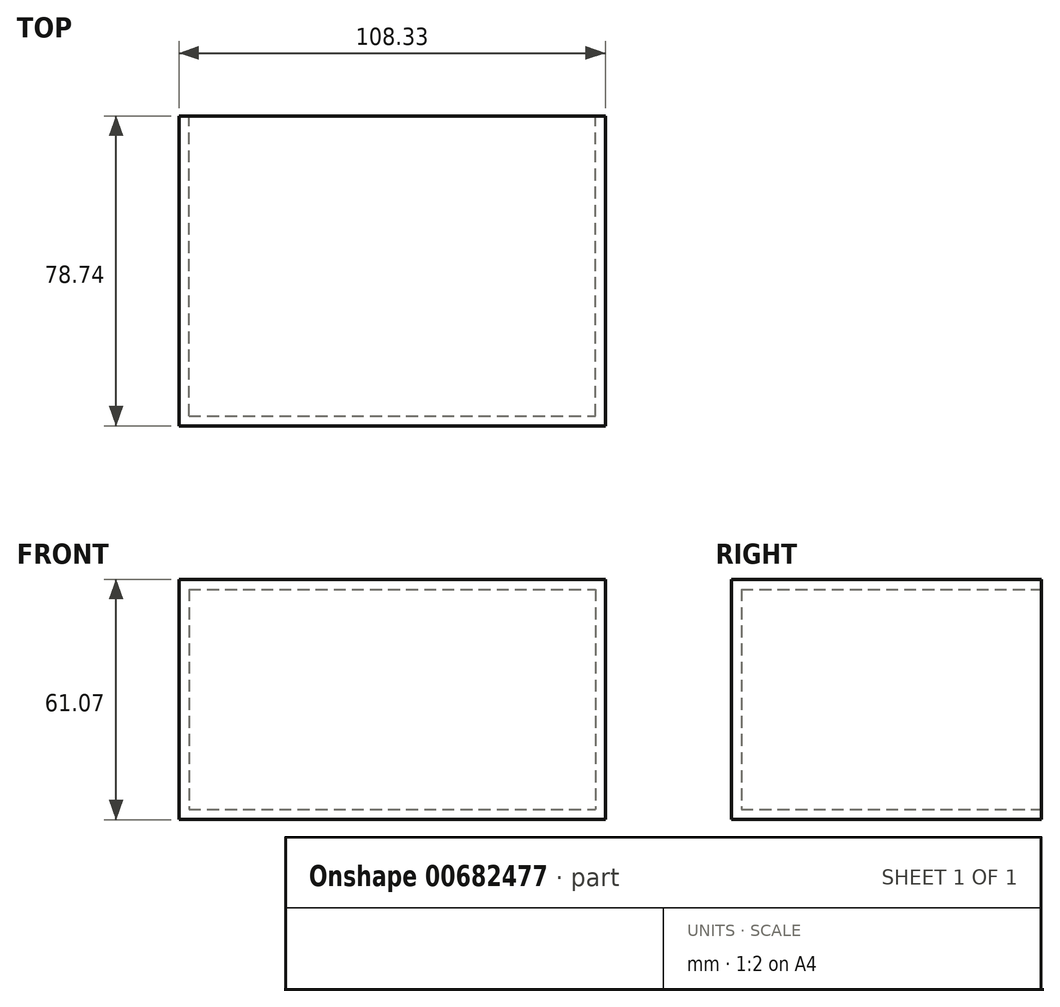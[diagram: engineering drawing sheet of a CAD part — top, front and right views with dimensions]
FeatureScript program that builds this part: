
annotation { "Feature Type Name" : "Feature", "Feature Type Description" : "" }
export const myFeature = defineFeature(function(context is Context, id is Id, definition is map)
    precondition{}
    {
        {
            var Q0;
            Q0=qCreatedBy(makeId("Front.planeOp"),FACE);
            var sketch = newSketch(context, id + "F0", { "sketchPlane" : qUnion([Q0])});
            skLineSegment(sketch, "E0.bottom", {"start": v(-61.13, 40) * mm, "end": v(42.12, 40) * mm});
            skLineSegment(sketch, "E0.top", {"start": v(-61.13, -15.98) * mm, "end": v(42.12, -15.98) * mm});
            skLineSegment(sketch, "E0.left", {"start": v(-61.13, 40) * mm, "end": v(-61.13, -15.98) * mm});
            skLineSegment(sketch, "E0.right", {"start": v(42.12, 40) * mm, "end": v(42.12, -15.98) * mm});
            skSolve(sketch);
        }
        {
            var Q0;
            Q0=makeQuery(id+"F0.imprint","IMPRINT",FACE,{"disambiguationData":[TD([[makeQuery(id+"F0.imprint","IMPRINT",EDGE,{"derivedFrom":sQuery(id+"F0.wireOp",EDGE,"E0.bottom")}),-1.0]])]});
            extrude(context, id + "F1", {"entities" : qUnion([Q0]), "depth" : 76.2 * mm, "offsetDistance" : 25.4 * mm});
        }
        {
            var Q0;
            Q0=makeQuery(id+"F1.opExtrude","CAP_FACE",FACE,{"disambiguationData":[OSD([sQuery(id+"F0.wireOp",EDGE,"E0.bottom"),sQuery(id+"F0.wireOp",EDGE,"E0.top"),sQuery(id+"F0.wireOp",EDGE,"E0.left"),sQuery(id+"F0.wireOp",EDGE,"E0.right")])],"isStart":true});
            shell(context, id + "F2", {"entities" : qUnion([Q0]), "thickness" : 2.54 * mm, "oppositeDirection" : true});
        }
    });
